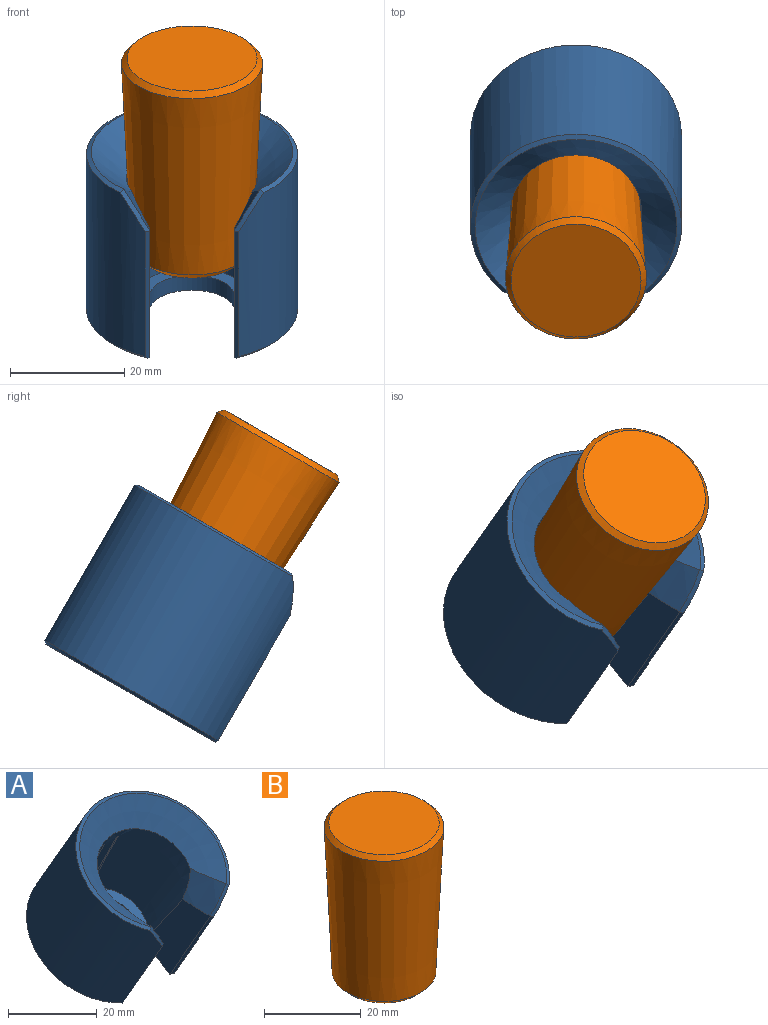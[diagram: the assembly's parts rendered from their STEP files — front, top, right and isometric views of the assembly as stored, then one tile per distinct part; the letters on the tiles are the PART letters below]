
ASSEMBLY  parts=2 mates=1
PART A: 48 faces, bbox 37.7x49.2x45.7 mm
  f0: cone r=11.5mm half-angle=3.6deg, axis (0,-0.5,0.87), area 1170.6mm2, adj f4,f8,f9,f11,f13,f14,f15,f16
  f1: plane 3.62x0.11mm, normal (0,0.5,-0.87), area 0.4mm2, adj f2,f3,f23,f27
  f2: plane 1.89x1.06mm, normal (1,0,0), area 0.1mm2, adj f1,f23,f27
  f3: plane 1.89x1.06mm, normal (-1,0,0), area 0.1mm2, adj f1,f23,f27
  f4: cone r=18.5mm half-angle=49.4deg, axis (0,-0.5,0.87), area 531.9mm2, adj f0,f13,f14,f44,f46,f47
  f5: cylinder r=18.5mm len=46.08mm, axis (0,0.5,-0.87), area 3083mm2, adj f42,f43,f44,f45,f46,f47
  f6: plane 36x29.67mm, normal (0,0.5,-0.87), area 667.5mm2, adj f7,f9,f11,f42,f43,f45
  f7: cylinder r=7.5mm len=15mm, axis (0,0.5,-0.87), area 70.7mm2, adj f6,f8,f10,f12
  f8: plane 20x14.39mm, normal (0,-0.5,0.87), area 91.4mm2, adj f0,f7,f9,f11
  f9: plane 27.66x23.48mm, normal (1,0,0), area 225.8mm2, adj f0,f6,f8,f10,f14,f45,f47
  f10: plane 2.6x1.5mm, normal (0,-0.87,-0.5), area 0mm2, adj f7,f9
  f11: plane 27.66x23.48mm, normal (-1,0,0), area 225.8mm2, adj f0,f6,f8,f12,f13,f42,f44
  f12: plane 2.6x1.5mm, normal (0,-0.87,-0.5), area 0mm2, adj f7,f11
  f13: bspline ~17.51x7.64mm, area 73.7mm2, adj f0,f4,f11,f44
  f14: bspline ~17.51x7.64mm, area 73.7mm2, adj f0,f4,f9,f47
  f15: plane 3.62x1.36mm, normal (0,0.5,-0.87), area 5.3mm2, adj f0,f16,f22,f26
  f16: plane 18.92x10.38mm, normal (1,0,0), area 30.6mm2, adj f0,f15,f17,f26
  f17: plane 1.46x0.85mm, normal (0,0.5,-0.87), area 0.8mm2, adj f0,f16,f18,f23,f25
  f18: plane 19.49x11.86mm, normal (-1,0,0), area 48.8mm2, adj f0,f17,f19,f23
  f19: plane 4.62x2.61mm, normal (0,-0.5,0.87), area 13.1mm2, adj f0,f18,f20,f23
  f20: plane 19.49x11.86mm, normal (1,0,0), area 48.8mm2, adj f0,f19,f21,f23
  f21: plane 1.46x0.85mm, normal (0,0.5,-0.87), area 0.8mm2, adj f0,f20,f22,f23,f24
  f22: plane 18.92x10.38mm, normal (-1,0,0), area 30.6mm2, adj f0,f15,f21,f26
  f23: plane 17.97x10.37mm, normal (0,-0.87,-0.5), area 22.6mm2, adj f1,f2,f3,f17,f18,f19,f20,f21
  f24: plane 16.79x9.51mm, normal (1,0,0), area 10.3mm2, adj f21,f23,f26,f27,f28
  f25: plane 16.79x9.51mm, normal (-1,0,0), area 10.3mm2, adj f17,f23,f26,f27,f28
  f26: plane 18.75x9.43mm, normal (0,0.89,0.45), area 75.9mm2, adj f15,f16,f22,f24,f25,f28
  f27: plane 18.68x9.4mm, normal (0,-0.89,-0.45), area 75.7mm2, adj f1,f2,f3,f24,f25,f28
  f28: plane 3.62x1.06mm, normal (0,0.45,-0.89), area 4.3mm2, adj f24,f25,f26,f27
  f29: plane 1.07x0.01mm, normal (0,0.5,-0.87), area 0mm2, adj f0,f41
  f30: plane 0.93x0.52mm, normal (1,0,0), area 0mm2, adj f0,f35,f40,f41
  f31: plane 0.93x0.52mm, normal (-1,0,0), area 0mm2, adj f0,f34,f36,f41
  f32: plane 1.69x0.1mm, normal (0,-0.5,0.87), area 0.2mm2, adj f0,f36,f38,f40
  f33: plane 1.89x0.38mm, normal (0,-0.87,-0.5), area 0.8mm2, adj f34,f35,f38,f41
  f34: cylinder r=0.5mm len=1.14mm, axis (0,-0.5,0.87), area 0.6mm2, adj f31,f33,f37,f41
  f35: cylinder r=0.5mm len=1.14mm, axis (0,0.5,-0.87), area 0.6mm2, adj f30,f33,f39,f41
  f36: cylinder r=0.6mm len=0.61mm, axis (0,0.87,0.5), area 0.1mm2, adj f0,f31,f32,f37
  f37: bspline ~0.94x0.6mm, area 0.3mm2, adj f34,f36,f38
  f38: cylinder r=0.6mm len=1.89mm, axis (1,0,0), area 1.7mm2, adj f32,f33,f37,f39
  f39: bspline ~0.94x0.6mm, area 0.3mm2, adj f35,f38,f40
  f40: cylinder r=0.6mm len=0.61mm, axis (0,-0.87,-0.5), area 0.1mm2, adj f0,f30,f32,f39
  f41: cylinder r=0.6mm len=2.89mm, axis (-1,0,0), area 2.3mm2, adj f0,f29,f30,f31,f33,f34,f35
  f42: plane 22.3x13.25mm, normal (-0.53,-0.74,-0.42), area 21.7mm2, adj f5,f6,f11,f43,f44
  f43: cone r=18mm half-angle=45deg, axis (0,-0.5,0.87), area 69.4mm2, adj f5,f6,f42,f45
  f44: bspline ~8.39x5.68mm, area 7.7mm2, adj f4,f5,f11,f13,f42,f46
  f45: plane 22.3x13.25mm, normal (0.53,-0.74,-0.42), area 21.7mm2, adj f5,f6,f9,f43,f47
  f46: cone r=18.5mm half-angle=65.3deg, axis (0,0.5,-0.87), area 78.7mm2, adj f4,f5,f44,f47
  f47: bspline ~8.39x5.68mm, area 7.7mm2, adj f4,f5,f9,f14,f45,f46
PART B: 5 faces, bbox 24.7x24.7x39.1 mm
  f0: cone r=12.4mm half-angle=2.6deg, axis (0,0,1), area 2655.7mm2, adj f3,f4
  f1: plane 22.8x22.8mm, normal (0,0,1), area 408.3mm2, adj f3
  f2: plane 18.3x18.3mm, normal (0,0,-1), area 263mm2, adj f4
  f3: cone r=11.4mm half-angle=43.7deg, axis (0,0,-1), area 103.2mm2, adj f0,f1
  f4: cone r=10.72mm half-angle=46.3deg, axis (0,0,1), area 135.3mm2, adj f0,f2
PLACE A t=(1.98,35.92,114.94)mm fixed
PLACE B rot(axis=(1,0,0),30deg) t=(1.98,47.98,-26.14)mm
MATE slider B.f0 <-> A.f4  axis (0,-0.5,0.87) through (1.98,13.08,34.31)mm
